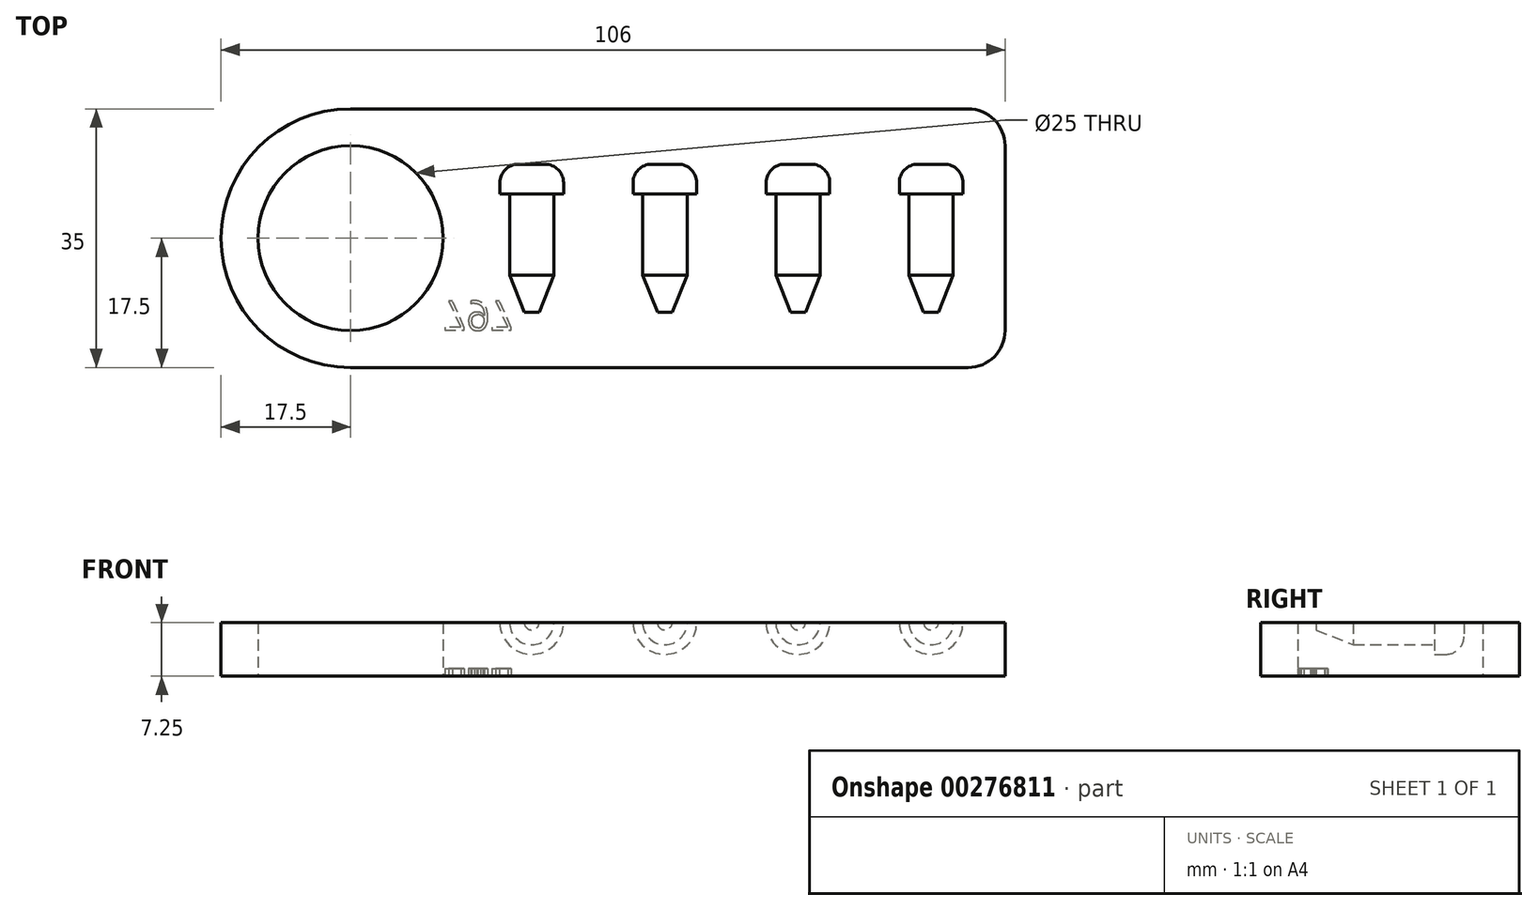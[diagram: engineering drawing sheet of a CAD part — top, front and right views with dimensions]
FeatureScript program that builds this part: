
annotation { "Feature Type Name" : "Feature", "Feature Type Description" : "" }
export const myFeature = defineFeature(function(context is Context, id is Id, definition is map)
    precondition{}
    {
        {
            var Q0;
            Q0=qCreatedBy(makeId("Top.planeOp"),FACE);
            var sketch = newSketch(context, id + "F0", { "sketchPlane" : qUnion([Q0])});
            skLineSegment(sketch, "E0.bottom", {"start": v(17.5, 0) * mm, "end": v(101, 0) * mm});
            skLineSegment(sketch, "E0.top", {"start": v(17.5, 35) * mm, "end": v(101, 35) * mm});
            skLineSegment(sketch, "E0.left", {"start": v(0, 17.5) * mm, "end": v(0, 17.5) * mm});
            skLineSegment(sketch, "E0.right", {"start": v(106, 5) * mm, "end": v(106, 30) * mm});
            skLineSegment(sketch, "E1.bottom", {"start": v(0, 0) * mm, "end": v(17.5, 0) * mm, "construction": true});
            skLineSegment(sketch, "E1.top", {"start": v(0, 17.5) * mm, "end": v(17.5, 17.5) * mm, "construction": true});
            skLineSegment(sketch, "E1.left", {"start": v(0, 0) * mm, "end": v(0, 17.5) * mm, "construction": true});
            skLineSegment(sketch, "E1.right", {"start": v(17.5, 0) * mm, "end": v(17.5, 17.5) * mm, "construction": true});
            skCircle(sketch, "E2", {"center": v(17.5, 17.5) * mm, "radius": 12.5 * mm});
            skPoint(sketch, "E3.visualSharp", {"position": v(0, 0) * mm});
            skArc(sketch, "E3.filletArc", {"start": v(0, 17.5) * mm, "mid": v(5.13, 5.13) * mm, "end": v(17.5, 0) * mm});
            skPoint(sketch, "E4.visualSharp", {"position": v(0, 35) * mm});
            skArc(sketch, "E4.filletArc", {"start": v(17.5, 35) * mm, "mid": v(5.13, 29.87) * mm, "end": v(0, 17.5) * mm});
            skPoint(sketch, "E5.visualSharp", {"position": v(106, 35) * mm});
            skArc(sketch, "E5.filletArc", {"start": v(106, 30) * mm, "mid": v(104.54, 33.54) * mm, "end": v(101, 35) * mm});
            skPoint(sketch, "E6.visualSharp", {"position": v(106, 0) * mm});
            skArc(sketch, "E6.filletArc", {"start": v(101, 0) * mm, "mid": v(104.54, 1.46) * mm, "end": v(106, 5) * mm});
            skSolve(sketch);
        }
        {
            var Q0;
            Q0=makeQuery(id+"F0.imprint","IMPRINT",FACE,{"disambiguationData":[TD([[makeQuery(id+"F0.imprint","IMPRINT",EDGE,{"derivedFrom":sQuery(id+"F0.wireOp",EDGE,"E0.bottom")}),1.0]])]});
            extrude(context, id + "F1", {"entities" : qUnion([Q0]), "depth" : 7.25 * mm, "offsetDistance" : 25 * mm});
        }
        {
            var Q0;
            Q0=makeQuery(id+"F1.opExtrude","CAP_FACE",FACE,{"disambiguationData":[OSD([sQuery(id+"F0.wireOp",EDGE,"E0.bottom"),sQuery(id+"F0.wireOp",EDGE,"E0.top"),sQuery(id+"F0.wireOp",EDGE,"E0.right"),sQuery(id+"F0.wireOp",EDGE,"E2"),sQuery(id+"F0.wireOp",EDGE,"E3.filletArc"),sQuery(id+"F0.wireOp",EDGE,"E4.filletArc"),sQuery(id+"F0.wireOp",EDGE,"E5.filletArc"),sQuery(id+"F0.wireOp",EDGE,"E6.filletArc")])],"isStart":false});
            var sketch = newSketch(context, id + "F2", { "sketchPlane" : qUnion([Q0])});
            skLineSegment(sketch, "E7.bottom", {"start": v(0, 0) * mm, "end": v(42, 0) * mm, "construction": true});
            skLineSegment(sketch, "E7.top", {"start": v(0, 7.5) * mm, "end": v(42, 7.5) * mm, "construction": true});
            skLineSegment(sketch, "E7.left", {"start": v(0, 0) * mm, "end": v(0, 7.5) * mm, "construction": true});
            skLineSegment(sketch, "E7.right", {"start": v(42, 0) * mm, "end": v(42, 7.5) * mm, "construction": true});
            skLineSegment(sketch, "E8", {"start": v(42, 7.5) * mm, "end": v(60, 7.5) * mm, "construction": true});
            skLineSegment(sketch, "E9", {"start": v(42, 7.5) * mm, "end": v(42, 23.5) * mm});
            skLineSegment(sketch, "E10", {"start": v(60, 7.5) * mm, "end": v(60, 23.5) * mm});
            skLineSegment(sketch, "E11", {"start": v(60, 7.5) * mm, "end": v(61, 7.5) * mm});
            skLineSegment(sketch, "E12", {"start": v(42, 7.5) * mm, "end": v(43, 7.5) * mm});
            skLineSegment(sketch, "E13.bottom", {"start": v(42, 27.5) * mm, "end": v(43.8, 27.5) * mm});
            skLineSegment(sketch, "E13.top", {"start": v(45, 23.5) * mm, "end": v(46.3, 23.5) * mm});
            skLineSegment(sketch, "E13.left", {"start": v(42, 27.5) * mm, "end": v(42, 23.5) * mm});
            skLineSegment(sketch, "E13.right", {"start": v(46.3, 25) * mm, "end": v(46.3, 23.5) * mm});
            skLineSegment(sketch, "E14.bottom", {"start": v(60, 27.5) * mm, "end": v(61.8, 27.5) * mm});
            skLineSegment(sketch, "E14.top", {"start": v(63, 23.5) * mm, "end": v(64.3, 23.5) * mm});
            skLineSegment(sketch, "E14.left", {"start": v(60, 27.5) * mm, "end": v(60, 23.5) * mm});
            skLineSegment(sketch, "E14.right", {"start": v(64.3, 25) * mm, "end": v(64.3, 23.5) * mm});
            skLineSegment(sketch, "E15.left", {"start": v(42, 23.5) * mm, "end": v(42, 10.5) * mm});
            skLineSegment(sketch, "E15.right", {"start": v(45, 23.5) * mm, "end": v(45, 12.5) * mm});
            skLineSegment(sketch, "E16.left", {"start": v(60, 23.5) * mm, "end": v(60, 10.5) * mm});
            skLineSegment(sketch, "E16.right", {"start": v(63, 23.5) * mm, "end": v(63, 12.5) * mm});
            skLineSegment(sketch, "E17", {"start": v(43, 7.5) * mm, "end": v(45, 12.5) * mm});
            skLineSegment(sketch, "E18", {"start": v(61, 7.5) * mm, "end": v(63, 12.5) * mm});
            skPoint(sketch, "E19.visualSharp", {"position": v(46.3, 27.5) * mm});
            skArc(sketch, "E19.filletArc", {"start": v(46.3, 25) * mm, "mid": v(45.57, 26.77) * mm, "end": v(43.8, 27.5) * mm});
            skPoint(sketch, "E20.visualSharp", {"position": v(64.3, 27.5) * mm});
            skArc(sketch, "E20.filletArc", {"start": v(64.3, 25) * mm, "mid": v(63.57, 26.77) * mm, "end": v(61.8, 27.5) * mm});
            skLineSegment(sketch, "E21", {"start": v(60, 7.5) * mm, "end": v(78, 7.5) * mm, "construction": true});
            skLineSegment(sketch, "E22", {"start": v(78, 7.5) * mm, "end": v(96, 7.5) * mm, "construction": true});
            skLineSegment(sketch, "E23", {"start": v(96, 7.5) * mm, "end": v(97, 7.5) * mm});
            skLineSegment(sketch, "E24", {"start": v(78, 7.5) * mm, "end": v(79, 7.5) * mm});
            skLineSegment(sketch, "E25", {"start": v(78, 7.5) * mm, "end": v(78, 27.5) * mm});
            skLineSegment(sketch, "E26", {"start": v(96, 7.5) * mm, "end": v(96, 23.5) * mm});
            skLineSegment(sketch, "E27.bottom", {"start": v(78, 27.5) * mm, "end": v(79.8, 27.5) * mm});
            skLineSegment(sketch, "E27.top", {"start": v(81, 23.5) * mm, "end": v(82.3, 23.5) * mm});
            skLineSegment(sketch, "E27.right", {"start": v(82.3, 25) * mm, "end": v(82.3, 23.5) * mm});
            skLineSegment(sketch, "E28.bottom", {"start": v(96, 27.5) * mm, "end": v(97.8, 27.5) * mm});
            skLineSegment(sketch, "E28.top", {"start": v(99, 23.5) * mm, "end": v(100.3, 23.5) * mm});
            skLineSegment(sketch, "E28.left", {"start": v(96, 27.5) * mm, "end": v(96, 23.5) * mm});
            skLineSegment(sketch, "E28.right", {"start": v(100.3, 25) * mm, "end": v(100.3, 23.5) * mm});
            skLineSegment(sketch, "E29.left", {"start": v(78, 23.5) * mm, "end": v(78, 12.5) * mm});
            skLineSegment(sketch, "E29.right", {"start": v(81, 23.5) * mm, "end": v(81, 12.5) * mm});
            skLineSegment(sketch, "E30.left", {"start": v(96, 23.5) * mm, "end": v(96, 10.5) * mm});
            skLineSegment(sketch, "E30.right", {"start": v(99, 23.5) * mm, "end": v(99, 12.5) * mm});
            skLineSegment(sketch, "E31", {"start": v(99, 12.5) * mm, "end": v(97, 7.5) * mm});
            skLineSegment(sketch, "E32", {"start": v(81, 12.5) * mm, "end": v(79, 7.5) * mm});
            skPoint(sketch, "E33.visualSharp", {"position": v(82.3, 27.5) * mm});
            skArc(sketch, "E33.filletArc", {"start": v(82.3, 25) * mm, "mid": v(81.57, 26.77) * mm, "end": v(79.8, 27.5) * mm});
            skPoint(sketch, "E34.visualSharp", {"position": v(100.3, 27.5) * mm});
            skArc(sketch, "E34.filletArc", {"start": v(100.3, 25) * mm, "mid": v(99.57, 26.77) * mm, "end": v(97.8, 27.5) * mm});
            skSolve(sketch);
        }
        {
            var Q0;
            Q0=makeQuery(id+"F2.imprint","IMPRINT",FACE,{"disambiguationData":[TD([[makeQuery(id+"F2.imprint","IMPRINT",EDGE,{"derivedFrom":sQuery(id+"F2.wireOp",EDGE,"E9")}),-1.0]])]});
            var Q1;
            Q1=sQuery(id+"F2.wireOp",EDGE,"E9");
            revolve(context, id + "F3", {"operationType" : NewBodyOperationType.REMOVE, "entities" : qUnion([Q0]), "axis" : qUnion([Q1]), "revolveType" : RevolveType.FULL, "oppositeDirection" : true});
        }
        {
            var Q0;
            Q0=makeQuery(id+"F2.imprint","IMPRINT",FACE,{"disambiguationData":[TD([[makeQuery(id+"F2.imprint","IMPRINT",EDGE,{"derivedFrom":sQuery(id+"F2.wireOp",EDGE,"E10")}),-1.0]])]});
            var Q1;
            Q1=sQuery(id+"F2.wireOp",EDGE,"E10");
            revolve(context, id + "F4", {"operationType" : NewBodyOperationType.REMOVE, "entities" : qUnion([Q0]), "axis" : qUnion([Q1]), "revolveType" : RevolveType.FULL, "oppositeDirection" : true});
        }
        {
            var Q0;
            {var subQ2=sQuery(id+"F2.wireOp",EDGE,"E24");Q0=makeQuery(id+"F2.imprint","IMPRINT",FACE,{"disambiguationData":[TD([[makeQuery(id+"F2.imprint","IMPRINT",EDGE,{"derivedFrom":subQ2}),1.0]])]});}
            var Q1;
            Q1=sQuery(id+"F2.wireOp",EDGE,"E29.left");
            revolve(context, id + "F5", {"operationType" : NewBodyOperationType.REMOVE, "entities" : qUnion([Q0]), "axis" : qUnion([Q1]), "revolveType" : RevolveType.FULL, "oppositeDirection" : true});
        }
        {
            var Q0;
            Q0=makeQuery(id+"F2.imprint","IMPRINT",FACE,{"disambiguationData":[TD([[makeQuery(id+"F2.imprint","IMPRINT",EDGE,{"derivedFrom":sQuery(id+"F2.wireOp",EDGE,"E23")}),1.0]])]});
            var Q1;
            Q1=sQuery(id+"F2.wireOp",EDGE,"E26");
            revolve(context, id + "F6", {"operationType" : NewBodyOperationType.REMOVE, "entities" : qUnion([Q0]), "axis" : qUnion([Q1]), "revolveType" : RevolveType.FULL, "oppositeDirection" : true});
        }
        {
            var Q0;
            Q0=makeQuery(id+"F1.opExtrude","CAP_FACE",FACE,{"disambiguationData":[OSD([sQuery(id+"F0.wireOp",EDGE,"E0.bottom"),sQuery(id+"F0.wireOp",EDGE,"E0.top"),sQuery(id+"F0.wireOp",EDGE,"E0.right"),sQuery(id+"F0.wireOp",EDGE,"E2"),sQuery(id+"F0.wireOp",EDGE,"E3.filletArc"),sQuery(id+"F0.wireOp",EDGE,"E4.filletArc"),sQuery(id+"F0.wireOp",EDGE,"E5.filletArc"),sQuery(id+"F0.wireOp",EDGE,"E6.filletArc")])],"isStart":true});
            var sketch = newSketch(context, id + "F7", { "sketchPlane" : qUnion([Q0])});
            skText(sketch, "E35", { "text": "797", "fontName": "OpenSans-Regular.ttf"});
            skLineSegment(sketch, "E36", {"start": v(39.6, -15.5) * mm, "end": v(39.6, -17.5) * mm});
            skLineSegment(sketch, "E37.bottom", {"start": v(0, 0) * mm, "end": v(30, 0) * mm, "construction": true});
            skLineSegment(sketch, "E37.top", {"start": v(0, -5) * mm, "end": v(30, -5) * mm, "construction": true});
            skLineSegment(sketch, "E37.left", {"start": v(0, 0) * mm, "end": v(0, -5) * mm, "construction": true});
            skLineSegment(sketch, "E37.right", {"start": v(30, 0) * mm, "end": v(30, -5) * mm, "construction": true});
            const initialGuessF7  = {"E35": [0.03, -0.009, 1, 0, 0.004]};
            skSetInitialGuess(sketch, initialGuessF7);
            skSolve(sketch);
        }
        {
            var Q0;
            Q0 = qSketchRegion(id + "F7", true);
            extrude(context, id + "F8", {"entities" : qUnion([Q0]), "operationType" : NewBodyOperationType.REMOVE, "oppositeDirection" : true, "depth" : 1 * mm});
        }
    });
